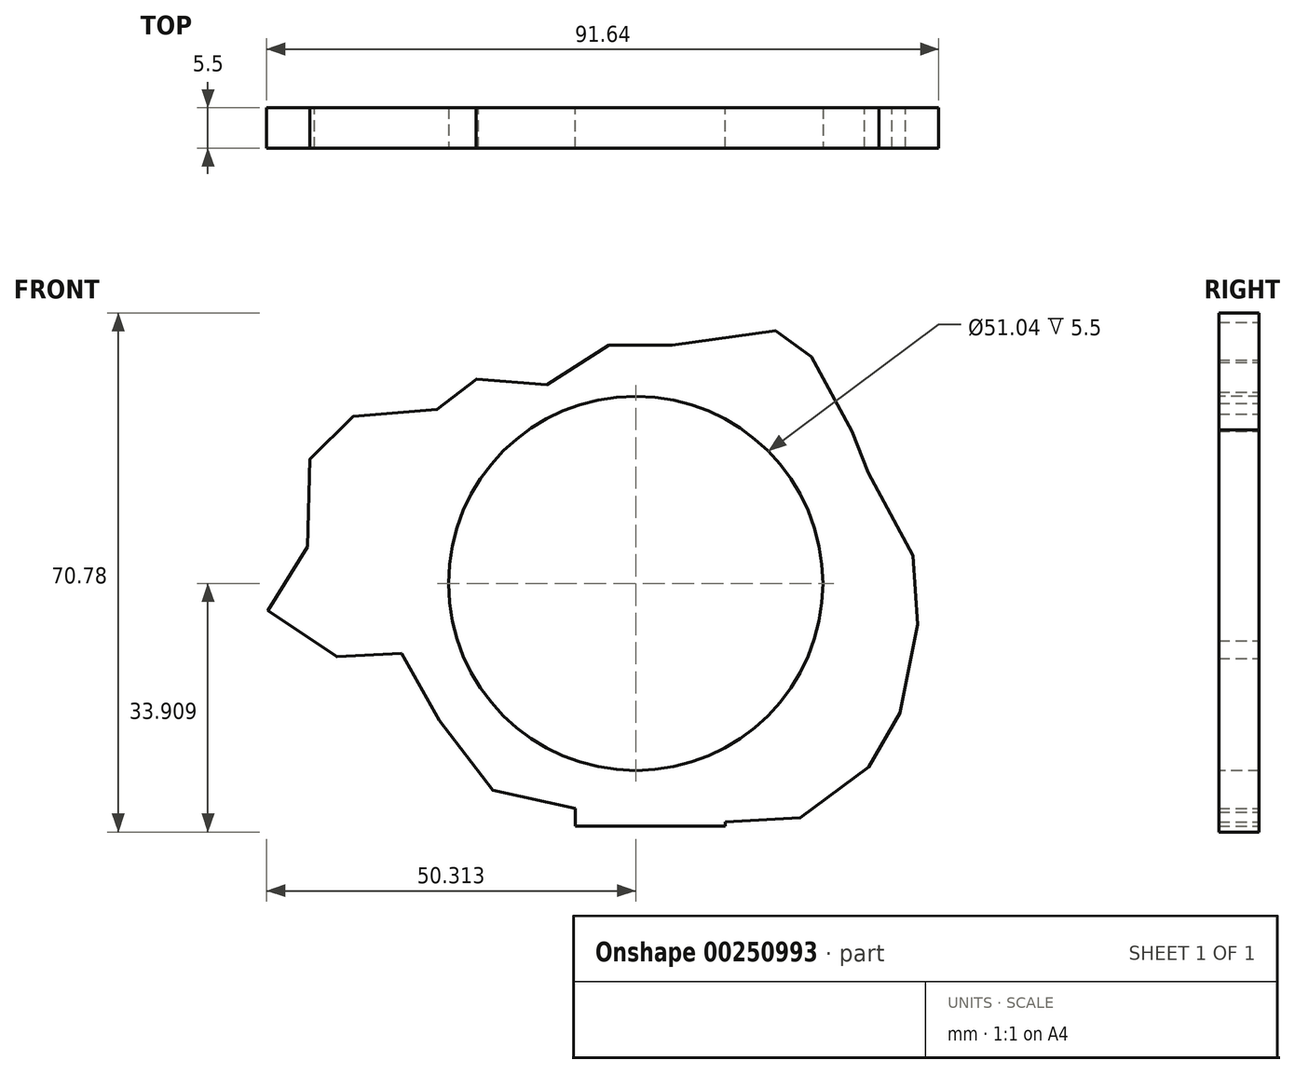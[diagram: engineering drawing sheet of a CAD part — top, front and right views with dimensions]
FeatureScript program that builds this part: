
annotation { "Feature Type Name" : "Feature", "Feature Type Description" : "" }
export const myFeature = defineFeature(function(context is Context, id is Id, definition is map)
    precondition{}
    {
        {
            var Q0;
            Q0=qCreatedBy(makeId("Front.planeOp"),FACE);
            var sketch = newSketch(context, id + "F0", { "sketchPlane" : qUnion([Q0])});
            skFitSpline(sketch, "E0", {"points": [v(-40.45, 14.1) * mm, v(-49.01, 11.24) * mm, v(-52.9, 7.35) * mm, v(-52.9, -4.59) * mm, v(-58.87, -12.1) * mm, v(-52.12, -20.68) * mm, v(-42.53, -18.34) * mm, v(-38.38, -24.57) * mm, v(-32.93, -32.36) * mm, v(-24.38, -41.19) * mm, v(-11.4, -40.16) * mm, v(0, -41.72) * mm, v(11.67, -44.06) * mm, v(18.41, -37.58) * mm, v(28, -32.65) * mm, v(26.45, -21.75) * mm, v(32.68, -10.6) * mm, v(22.82, 0) * mm, v(24.38, 10.17) * mm, v(17.12, 11.2) * mm, v(14.52, 26.26) * mm, v(3.11, 20.04) * mm, v(-10.9, 24.98) * mm, v(-15.04, 15.9) * mm, v(-29.82, 19.54) * mm, v(-30.34, 13.3) * mm, v(-40.45, 14.1) * mm]});
            skLineSegment(sketch, "E1.bottom", {"start": v(3.62, -43.58) * mm, "end": v(-16.84, -43.58) * mm});
            skLineSegment(sketch, "E1.top", {"start": v(3.62, -41.15) * mm, "end": v(-16.84, -41.15) * mm});
            skLineSegment(sketch, "E1.left", {"start": v(3.62, -43.58) * mm, "end": v(3.62, -41.15) * mm});
            skLineSegment(sketch, "E1.right", {"start": v(-16.84, -43.58) * mm, "end": v(-16.84, -41.15) * mm});
            skSolve(sketch);
        }
        {
            var Q0;
            Q0 = qSketchRegion(id + "F0", true);
            extrude(context, id + "F1", {"entities" : qUnion([Q0]), "depth" : 5.5 * mm});
        }
        {
            var Q0;
            Q0=makeQuery(id+"F1.opExtrude","CAP_FACE",FACE,{"disambiguationData":[OSD([sQuery(id+"F0.wireOp",EDGE,"E0"),sQuery(id+"F0.wireOp",EDGE,"E1.bottom"),sQuery(id+"F0.wireOp",EDGE,"E1.left"),sQuery(id+"F0.wireOp",EDGE,"E1.right")])],"isStart":false});
            var sketch = newSketch(context, id + "F2", { "sketchPlane" : qUnion([Q0])});
            skCircle(sketch, "E2", {"center": v(-8.6, -10.47) * mm, "radius": 25.52 * mm});
            skSolve(sketch);
        }
        {
            var Q0;
            Q0=makeQuery(id+"F2.imprint","IMPRINT",FACE,{"disambiguationData":[TD([[makeQuery(id+"F2.imprint","IMPRINT",EDGE,{"derivedFrom":sQuery(id+"F2.wireOp",EDGE,"E2")}),1.0]])]});
            extrude(context, id + "F3", {"entities" : qUnion([Q0]), "operationType" : NewBodyOperationType.REMOVE, "oppositeDirection" : true, "depth" : 25 * mm});
        }
    });
